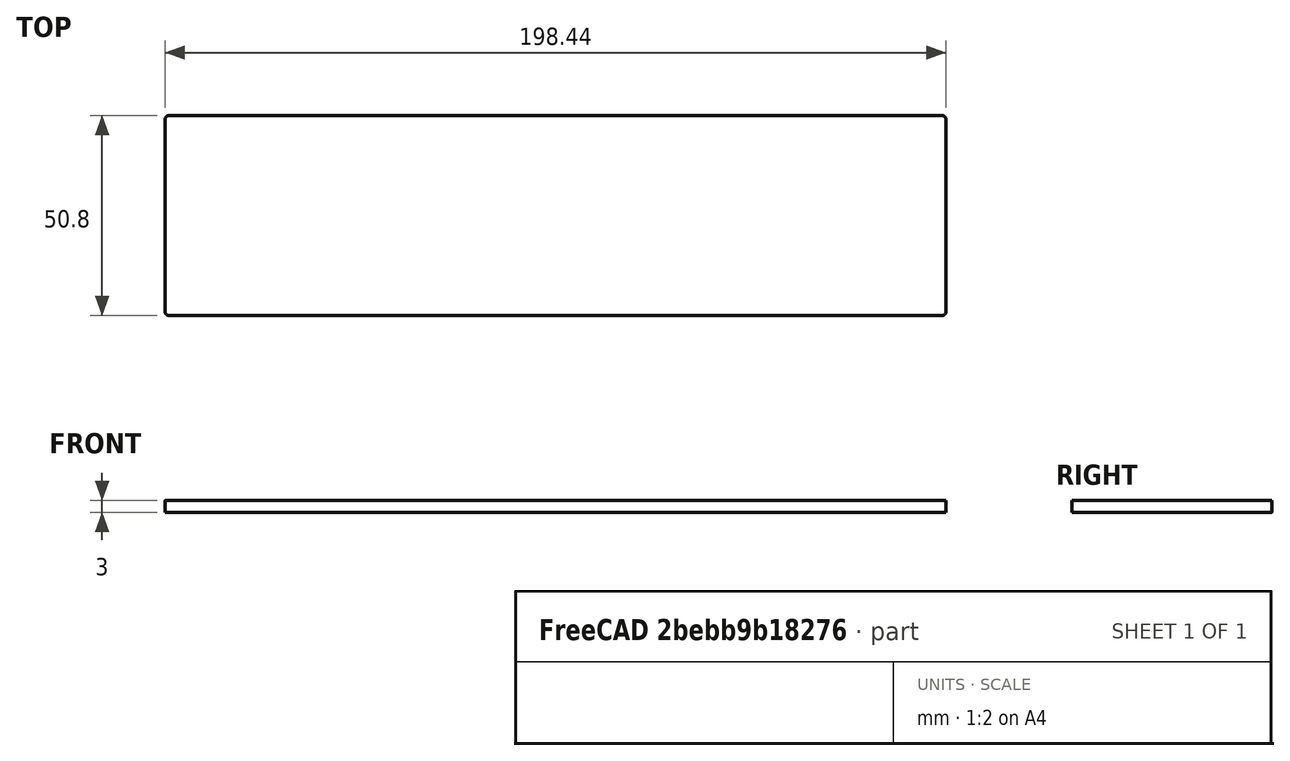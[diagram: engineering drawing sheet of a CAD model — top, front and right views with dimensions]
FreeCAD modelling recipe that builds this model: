
FCSTD DOCUMENT  (FreeCAD 0.20R29603 (Git))
Label: floor
License: All rights reserved
LicenseURL: http://en.wikipedia.org/wiki/All_rights_reserved
objects: Sketcher::SketchObject×2, Spreadsheet::Sheet×1, PartDesign::Pad×1, PartDesign::Body×1, Part::Part2DObjectPython×1
note: 6 computed .brp shape members not serialized (recipe doc carries the construction recipe); baked Part::Feature solids carry a one-line shape summary decoded from their .brp

FEATURE [Spreadsheet::Sheet] Spreadsheet
  cells = A2=Design Parameters; A3=Length; B3(Length)==7.8125in; A4=Width; B4(Width)==2in; A5=Thickness; B5(Thickness)==3mm; A6=FilletRadius; B6(FilletRadius)==1mm
FEATURE [Sketcher::SketchObject] Sketch  label="FloorSketch"
  FullyConstrained = true
  MapMode = 5
  Support = -> [XY_Plane]
  expr: Constraints[20] = Spreadsheet.FilletRadius
  expr: Constraints[21] = Spreadsheet.Length
  expr: Constraints[22] = Spreadsheet.Width
  sketch-geometry (10):
    g0: ArcOfCircle CenterX=1 CenterY=1 CenterZ=0 NormalX=0 NormalY=0 NormalZ=1 AngleXU=0 Radius=1 StartAngle=3.14159 EndAngle=4.71239
    g1: LineSegment StartX=6.06e-14 StartY=1 StartZ=0 EndX=6.06e-14 EndY=49.8 EndZ=0
    g2: ArcOfCircle CenterX=1 CenterY=49.8 CenterZ=0 NormalX=0 NormalY=0 NormalZ=1 AngleXU=0 Radius=1 StartAngle=1.5708 EndAngle=3.14159
    g3: LineSegment StartX=1 StartY=50.8 StartZ=0 EndX=197.438 EndY=50.8 EndZ=0
    g4: ArcOfCircle CenterX=197.437 CenterY=49.8 CenterZ=0 NormalX=0 NormalY=0 NormalZ=1 AngleXU=0 Radius=1 StartAngle=-2.16e-12 EndAngle=1.5708
    g5: LineSegment StartX=198.438 StartY=49.8 StartZ=0 EndX=198.438 EndY=1 EndZ=0
    g6: ArcOfCircle CenterX=197.437 CenterY=1 CenterZ=0 NormalX=0 NormalY=0 NormalZ=1 AngleXU=0 Radius=1 StartAngle=4.71239 EndAngle=6.28319
    g7: LineSegment StartX=197.438 StartY=9.439e-13 StartZ=0 EndX=1 EndY=9.439e-13 EndZ=0
    g8: GeomPoint X=0 Y=0 Z=0
    g9: GeomPoint X=198.438 Y=50.8 Z=0
  constraints (23):
    c: Tangent(g0,g1) = 1.5708
    c: Tangent(g1,g2) = 1.5708
    c: Tangent(g2,g3) = 1.5708
    c: Tangent(g3,g4) = 1.5708
    c: Tangent(g4,g5) = 1.5708
    c: Tangent(g5,g6) = 1.5708
    c: Tangent(g6,g7) = 1.5708
    c: Tangent(g7,g0) = 1.5708
    c: Horizontal(g3)
    c: Horizontal(g7)
    c: Vertical(g1)
    c: Vertical(g5)
    c: Equal(g0,g2)
    c: Equal(g2,g4)
    c: Equal(g4,g6)
    c: PointOnObject(g8,g1)
    c: PointOnObject(g8,g7)
    c: PointOnObject(g9,g3)
    c: PointOnObject(g9,g5)
    c: Coincident(g8,g-1)
    c: Radius(g4) = 1
    c: DistanceX(g0,g5) = 198.438
    c: DistanceY(g6,g3) = 50.8
FEATURE [PartDesign::Pad] Pad  label="FloorPad"
  Direction = (0,0,1)
  Length = 3
  Length2 = 10
  Profile = -> Sketch
  ReferenceAxis = -> Sketch [N_Axis]
  Type = 0
  expr: Length = Spreadsheet.Thickness
FEATURE [PartDesign::Body] Body
  Group = -> [Sketch,Pad]
  Origin = -> Origin
  Tip = -> Pad
FEATURE [Part::Part2DObjectPython] Shape2DView  # Draft 2D object (typed FeaturePython)
  AutoUpdate = true
  Base = -> Pad
  Clip = false
  FuseArch = false
  HiddenLines = false
  InPlace = true
  OnlySolids = false
  Projection = (0,0,1)
  ProjectionMode = 0
  SegmentLength = 0.05
  Tessellation = false
  VisibleOnly = false
FEATURE [Sketcher::SketchObject] Sketch001
  FullyConstrained = false
  sketch-geometry (8):
    g0: ArcOfCircle CenterX=1 CenterY=1 CenterZ=0 NormalX=0 NormalY=0 NormalZ=1 AngleXU=0 Radius=1 StartAngle=3.14159 EndAngle=4.71239
    g1: LineSegment StartX=197.438 StartY=9.439e-13 StartZ=0 EndX=1 EndY=9.439e-13 EndZ=0
    g2: ArcOfCircle CenterX=197.437 CenterY=1 CenterZ=0 NormalX=0 NormalY=0 NormalZ=1 AngleXU=0 Radius=1 StartAngle=4.71239 EndAngle=6.28319
    g3: LineSegment StartX=198.438 StartY=49.8 StartZ=0 EndX=198.438 EndY=1 EndZ=0
    g4: ArcOfCircle CenterX=197.437 CenterY=49.8 CenterZ=0 NormalX=0 NormalY=0 NormalZ=1 AngleXU=0 Radius=1 StartAngle=-2.16e-12 EndAngle=1.5708
    g5: LineSegment StartX=1 StartY=50.8 StartZ=0 EndX=197.438 EndY=50.8 EndZ=0
    g6: ArcOfCircle CenterX=1 CenterY=49.8 CenterZ=0 NormalX=0 NormalY=0 NormalZ=1 AngleXU=0 Radius=1 StartAngle=1.5708 EndAngle=3.14159
    g7: LineSegment StartX=6.06e-14 StartY=1 StartZ=0 EndX=6.06e-14 EndY=49.8 EndZ=0
